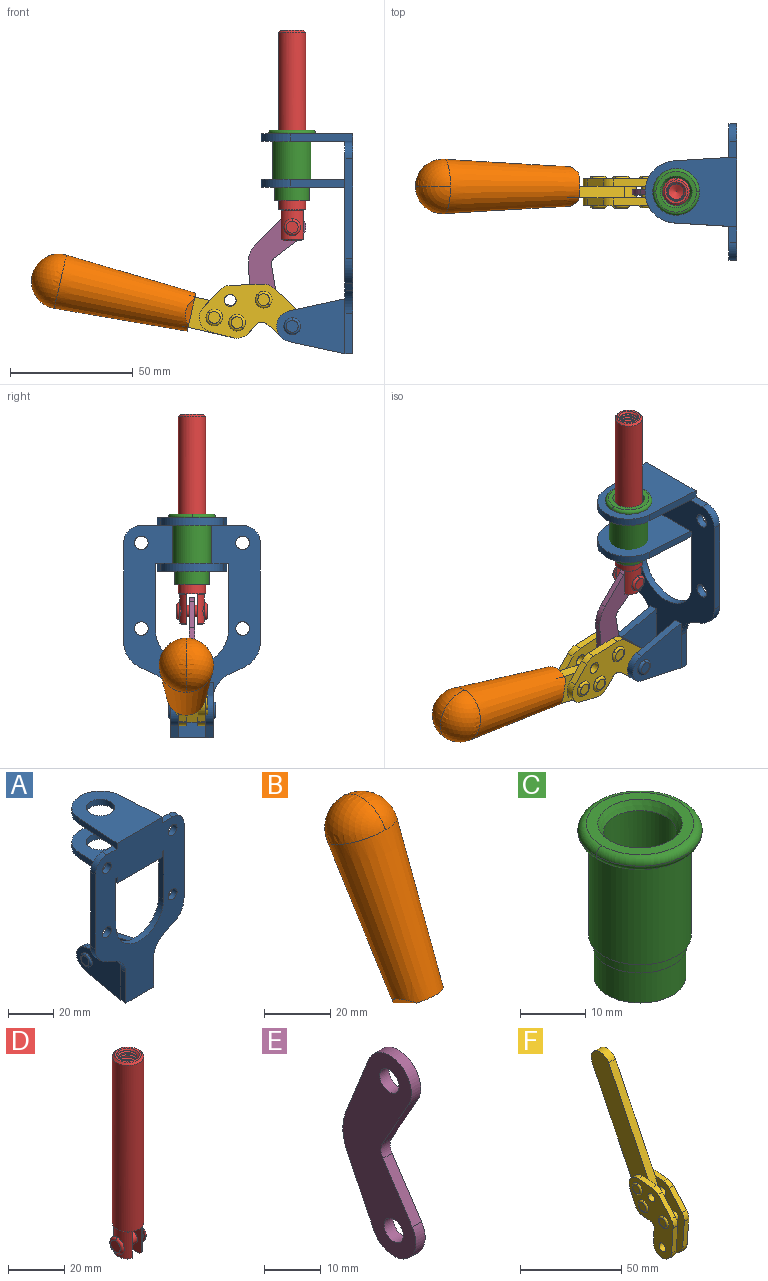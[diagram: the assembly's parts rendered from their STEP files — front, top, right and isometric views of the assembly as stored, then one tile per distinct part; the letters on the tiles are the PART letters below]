
ASSEMBLY  parts=6 mates=6
PART A: 55 faces, bbox 55.7x37.4x89.8 mm
  f0: torus R=2.41mm, axis (-1,0,0), area 15mm2, adj f11,f15,f25
  f1: torus R=2.41mm, axis (-1,0,0), area 15mm2, adj f10,f12,f22
  f2: cylinder r=2.78mm len=5.56mm, axis (0,-1,0), area 54.2mm2, adj f30,f54
  f3: cylinder r=14.99mm len=29.97mm, axis (0,-1,0), area 145.9mm2, adj f30,f49,f53,f54
  f4: cylinder r=2.78mm len=5.56mm, axis (0,-1,0), area 54.2mm2, adj f30,f54
  f5: cylinder r=2.78mm len=5.56mm, axis (0,-1,0), area 54.2mm2, adj f30,f54
  f6: cylinder r=2.78mm len=5.56mm, axis (0,-1,0), area 54.2mm2, adj f30,f54
  f7: cylinder r=6.35mm len=12.7mm, axis (0,0,1), area 123.6mm2, adj f27,f51
  f8: cylinder r=6.35mm len=12.7mm, axis (0,0,-1), area 124.7mm2, adj f21,f35
  f9: cylinder r=2.41mm len=11.18mm, axis (-1,0,0), area 169.4mm2, adj f16,f19
  f10: plane 4.83x4.83mm, normal (1,0,0), area 18.3mm2, adj f1,f12
  f11: plane 4.83x4.83mm, normal (-1,0,0), area 18.3mm2, adj f0,f15
  f12: torus R=2.41mm, axis (-1,0,0), area 15mm2, adj f1,f10,f22
  f13: cylinder r=6.35mm len=12.41mm, axis (1,0,0), area 53.4mm2, adj f18,f19,f22,f23
  f14: cylinder r=6.35mm len=12.41mm, axis (-1,0,0), area 53.4mm2, adj f16,f17,f24,f25
  f15: torus R=2.41mm, axis (-1,0,0), area 15mm2, adj f0,f11,f25
  f16: plane 27.86x22.35mm, normal (1,0,0), area 425.4mm2, adj f9,f14,f17,f24,f30
  f17: plane 22.86x4.97mm, normal (0,0.21,0.98), area 72.5mm2, adj f14,f16,f25,f30
  f18: plane 22.86x4.97mm, normal (0,0.21,0.98), area 72.5mm2, adj f13,f19,f22,f30
  f19: plane 27.86x22.35mm, normal (-1,0,0), area 425.4mm2, adj f9,f13,f18,f23,f30
  f20: cylinder r=12.7mm len=25.35mm, axis (0,0,-1), area 119.8mm2, adj f21,f34,f35,f36
  f21: plane 34.21x28.07mm, normal (0,0,-1), area 702.4mm2, adj f8,f20,f30,f34,f36
  f22: plane 27.96x22.45mm, normal (1,0,0), area 407.2mm2, adj f1,f12,f13,f18,f23,f30,f42,f43
  f23: plane 22.86x4.97mm, normal (0,0.21,-0.98), area 72.5mm2, adj f13,f19,f22,f44
  f24: plane 22.86x4.97mm, normal (0,0.21,-0.98), area 72.5mm2, adj f14,f16,f25,f44
  f25: plane 27.86x22.35mm, normal (-1,0,0), area 407.1mm2, adj f0,f14,f15,f17,f24,f30,f45,f46
  f26: plane 3.1x0.95mm, normal (0,0,-1), area 2.7mm2, adj f30,f49,f50,f54
  f27: plane 34.21x28.07mm, normal (0,0,1), area 702.4mm2, adj f7,f28,f30,f50,f52
  f28: cylinder r=12.7mm len=25.35mm, axis (0,0,1), area 118.8mm2, adj f27,f50,f51,f52
  f29: plane 3.1x0.95mm, normal (0,0,-1), area 2.7mm2, adj f30,f52,f53,f54
  f30: plane 86.54x55.63mm, normal (0,1,0), area 2362.9mm2, adj f2,f3,f4,f5,f6,f16,f17,f18
  f31: plane 40.56x3.1mm, normal (-1,0,0), area 125.7mm2, adj f30,f32,f48,f54
  f32: cylinder r=7.11mm len=7.11mm, axis (0,-1,0), area 34.6mm2, adj f30,f31,f33,f54
  f33: plane 6.67x3.1mm, normal (0,0,1), area 20.4mm2, adj f30,f32,f34,f54
  f34: plane 25.39x3.13mm, normal (-1,0.06,0), area 79.5mm2, adj f20,f21,f33,f35,f54
  f35: plane 37.31x28.45mm, normal (0,0,1), area 789.9mm2, adj f8,f20,f34,f36,f54
  f36: plane 25.39x3.13mm, normal (1,0.06,0), area 79.5mm2, adj f20,f21,f35,f37,f54
  f37: plane 6.67x3.1mm, normal (0,0,1), area 20.4mm2, adj f30,f36,f38,f54
  f38: cylinder r=7.11mm len=7.11mm, axis (0,-1,0), area 34.6mm2, adj f30,f37,f39,f54
  f39: plane 40.56x3.1mm, normal (1,0,0), area 125.7mm2, adj f30,f38,f40,f54
  f40: cylinder r=11.18mm len=10.16mm, axis (0,-1,0), area 39.5mm2, adj f30,f39,f41,f54
  f41: plane 6.09x3.1mm, normal (0.42,0,-0.91), area 20.8mm2, adj f30,f40,f42,f54
  f42: cylinder r=11.18mm len=9.41mm, axis (0,-1,0), area 37.2mm2, adj f22,f30,f41,f43,f54
  f43: plane 16.5x3.1mm, normal (1,0,0), area 51.1mm2, adj f22,f42,f44,f54
  f44: plane 17.37x3.1mm, normal (0,0,-1), area 53.8mm2, adj f23,f24,f30,f43,f45,f54
  f45: plane 16.5x3.1mm, normal (-1,0,0), area 51.1mm2, adj f25,f44,f46,f54
  f46: cylinder r=11.18mm len=9.41mm, axis (0,-1,0), area 37.2mm2, adj f25,f30,f45,f47,f54
  f47: plane 6.09x3.1mm, normal (-0.42,0,-0.91), area 20.8mm2, adj f30,f46,f48,f54
  f48: cylinder r=11.18mm len=10.16mm, axis (0,-1,0), area 39.5mm2, adj f30,f31,f47,f54
  f49: plane 26.54x3.1mm, normal (-1,0,0), area 82.3mm2, adj f3,f26,f30,f54
  f50: plane 25.39x3.1mm, normal (1,0.06,0), area 78.8mm2, adj f26,f27,f28,f51,f54
  f51: plane 37.31x28.45mm, normal (0,0,-1), area 789.9mm2, adj f7,f28,f50,f52,f54
  f52: plane 25.39x3.1mm, normal (-1,0.06,0), area 78.8mm2, adj f27,f28,f29,f51,f54
  f53: plane 26.54x3.1mm, normal (1,0,0), area 82.3mm2, adj f3,f29,f30,f54
  f54: plane 89.66x55.63mm, normal (0,-1,0), area 2678.5mm2, adj f2,f3,f4,f5,f6,f26,f29,f31
PART B: 11 faces, bbox 22.3x42.6x64.5 mm
  f0: sphere r=11.13mm, area 411.4mm2, adj f1,f8
  f1: cone r=11.11mm half-angle=3.3deg, axis (0,0.44,0.9), area 3251.8mm2, adj f0,f7,f8,f9,f10
  f2: cylinder r=6.16mm len=11.7mm, axis (1,0,0), area 89.5mm2, adj f3,f4,f5,f6
  f3: plane 60.23x36.75mm, normal (-1,0,0), area 763.6mm2, adj f2,f4,f6,f10
  f4: plane 51.37x25.05mm, normal (0,0.9,-0.44), area 264.2mm2, adj f2,f3,f5,f10
  f5: plane 60.23x36.75mm, normal (1,0,0), area 763.6mm2, adj f2,f4,f6,f10
  f6: plane 51.37x25.05mm, normal (0,-0.9,0.44), area 264.2mm2, adj f2,f3,f5,f10
  f7: plane 9.95x5.95mm, normal (0.71,-0.31,-0.64), area 25.8mm2, adj f1,f10
  f8: sphere r=11.13mm, area 411.4mm2, adj f0,f1
  f9: plane 9.95x5.95mm, normal (-0.71,-0.31,-0.64), area 25.8mm2, adj f1,f10
  f10: plane 14.27x11.38mm, normal (0,-0.44,-0.9), area 106.7mm2, adj f1,f3,f4,f5,f6,f7,f9
PART C: 15 faces, bbox 20.6x20.6x28.7 mm
  f0: torus R=8.26mm, axis (0,0,1), area 56.8mm2, adj f1,f10,f12
  f1: torus R=8.26mm, axis (0,0,1), area 56.8mm2, adj f0,f6,f13
  f2: cylinder r=5.59mm len=25.91mm, axis (0,0,1), area 909.6mm2, adj f3,f4
  f3: cone r=6.86mm half-angle=45deg, axis (0,0,-1), area 70.2mm2, adj f2,f14
  f4: cone r=6.47mm half-angle=30deg, axis (0,0,1), area 66.7mm2, adj f2,f13
  f5: cylinder r=7.04mm len=14.07mm, axis (0,0,1), area 252.6mm2, adj f11,f14
  f6: torus R=8.26mm, axis (0,0,1), area 56.8mm2, adj f1,f12,f13
  f7: cylinder r=7.16mm len=14.33mm, axis (0,0,1), area 91.5mm2, adj f9,f11
  f8: cylinder r=7.86mm len=18.42mm, axis (0,0,1), area 909.6mm2, adj f9,f10
  f9: plane 15.72x15.72mm, normal (0,0,-1), area 33mm2, adj f7,f8
  f10: plane 16.51x16.51mm, normal (0,0,-1), area 19.9mm2, adj f0,f8,f12
  f11: plane 14.33x14.33mm, normal (0,0,-1), area 5.7mm2, adj f5,f7
  f12: torus R=8.26mm, axis (0,0,1), area 56.8mm2, adj f0,f6,f10
  f13: plane 16.51x16.51mm, normal (0,0,1), area 82.7mm2, adj f1,f4,f6
  f14: plane 14.07x14.07mm, normal (0,0,-1), area 7.8mm2, adj f3,f5
PART D: 48 faces, bbox 12.6x11.1x86.1 mm
  f0: torus R=2.41mm, axis (-1,0,0), area 15mm2, adj f30,f32,f34
  f1: torus R=2.41mm, axis (-1,0,0), area 15mm2, adj f29,f31,f33
  f2: cylinder r=5.54mm len=72.39mm, axis (0,0,1), area 2518.5mm2, adj f3,f4,f42,f43
  f3: cone r=5.54mm half-angle=45deg, axis (0,0,1), area 7.6mm2, adj f2,f5,f41
  f4: cone r=5.54mm half-angle=45deg, axis (0,0,-1), area 34.9mm2, adj f2,f39
  f5: cylinder r=5.08mm len=11.48mm, axis (0,0,1), area 108.3mm2, adj f3,f7,f8,f41
  f6: cylinder r=2.41mm len=4.83mm, axis (-1,0,0), area 71.2mm2, adj f40,f41
  f7: cylinder r=2.41mm len=4.83mm, axis (-1,0,0), area 7.6mm2, adj f5,f34
  f8: cone r=5.08mm half-angle=45deg, axis (0,0,1), area 10.6mm2, adj f5,f37,f41
  f9: cone r=3.98mm half-angle=45deg, axis (0,0,1), area 17.6mm2, adj f27,f39,f45,f46,f47
  f10: cylinder r=2.41mm len=4.83mm, axis (-1,0,0), area 7.6mm2, adj f33,f38
  f11: cylinder r=3.2mm len=6.4mm, axis (0,0,1), area 78.4mm2, adj f12,f28,f44,f45,f47
  f12: cylinder r=3.2mm len=6.4mm, axis (0,0,1), area 10.5mm2, adj f11,f13,f45,f47
  f13: cylinder r=3.2mm len=6.4mm, axis (0,0,1), area 10.5mm2, adj f12,f14,f45,f47
  f14: cylinder r=3.2mm len=6.4mm, axis (0,0,1), area 10.5mm2, adj f13,f15,f45,f47
  f15: cylinder r=3.2mm len=6.4mm, axis (0,0,1), area 10.5mm2, adj f14,f16,f45,f47
  f16: cylinder r=3.2mm len=6.4mm, axis (0,0,1), area 10.5mm2, adj f15,f17,f45,f47
  f17: cylinder r=3.2mm len=6.4mm, axis (0,0,1), area 10.5mm2, adj f16,f18,f45,f47
  f18: cylinder r=3.2mm len=6.4mm, axis (0,0,1), area 10.5mm2, adj f17,f19,f45,f47
  f19: cylinder r=3.2mm len=6.4mm, axis (0,0,1), area 10.5mm2, adj f18,f20,f45,f47
  f20: cylinder r=3.2mm len=6.4mm, axis (0,0,1), area 10.5mm2, adj f19,f21,f45,f47
  f21: cylinder r=3.2mm len=6.4mm, axis (0,0,1), area 10.5mm2, adj f20,f22,f45,f47
  f22: cylinder r=3.2mm len=6.4mm, axis (0,0,1), area 10.5mm2, adj f21,f23,f45,f47
  f23: cylinder r=3.2mm len=6.4mm, axis (0,0,1), area 10.5mm2, adj f22,f24,f45,f47
  f24: cylinder r=3.2mm len=6.4mm, axis (0,0,1), area 10.5mm2, adj f23,f25,f45,f47
  f25: cylinder r=3.2mm len=6.4mm, axis (0,0,1), area 10.5mm2, adj f24,f26,f45,f47
  f26: cylinder r=3.2mm len=6.4mm, axis (0,0,1), area 10.5mm2, adj f25,f27,f45,f47
  f27: cylinder r=3.2mm len=6.4mm, axis (0,0,1), area 7.4mm2, adj f9,f26,f45,f47
  f28: cone r=3.2mm half-angle=60deg, axis (0,0,1), area 37.2mm2, adj f11
  f29: plane 4.83x4.83mm, normal (-1,0,0), area 18.3mm2, adj f1,f31
  f30: plane 4.83x4.83mm, normal (1,0,0), area 18.3mm2, adj f0,f32
  f31: torus R=2.41mm, axis (-1,0,0), area 15mm2, adj f1,f29,f33
  f32: torus R=2.41mm, axis (-1,0,0), area 15mm2, adj f0,f30,f34
  f33: plane 6.83x6.83mm, normal (1,0,0), area 18.3mm2, adj f1,f10,f31
  f34: plane 6.83x6.83mm, normal (-1,0,0), area 18.3mm2, adj f0,f7,f32
  f35: cone r=5.08mm half-angle=45deg, axis (0,0,1), area 10.6mm2, adj f36,f38,f40
  f36: plane 7.25x1.97mm, normal (0,0,-1), area 10mm2, adj f35,f40
  f37: plane 7.25x1.97mm, normal (0,0,-1), area 10mm2, adj f8,f41
  f38: cylinder r=5.08mm len=11.48mm, axis (0,0,1), area 108.3mm2, adj f10,f35,f40,f42
  f39: plane 9.55x9.55mm, normal (0,0,1), area 22mm2, adj f4,f9
  f40: plane 12.76x10.09mm, normal (1,0,0), area 95.7mm2, adj f6,f35,f36,f38,f42,f43
  f41: plane 12.76x10.09mm, normal (-1,0,0), area 95.7mm2, adj f3,f5,f6,f8,f37,f43
  f42: cone r=5.54mm half-angle=45deg, axis (0,0,1), area 7.6mm2, adj f2,f38,f40
  f43: plane 11.07x4.7mm, normal (0,0,-1), area 50.4mm2, adj f2,f40,f41
  f44: plane 0.89x0.62mm, normal (-1,0,0), area 0.3mm2, adj f11,f45,f46,f47
  f45: bspline ~24.8x7.63mm, area 266.6mm2, adj f9,f11,f12,f13,f14,f15,f16,f17
  f46: bspline ~24.87x7.63mm, area 73.6mm2, adj f9,f44,f45,f47
  f47: bspline ~24.98x7.63mm, area 272.5mm2, adj f9,f11,f12,f13,f14,f15,f16,f17
PART E: 12 faces, bbox 2.3x18.2x42.8 mm
  f0: cylinder r=2.4mm len=4.8mm, axis (1,0,0), area 34.9mm2, adj f4,f11
  f1: cylinder r=10.41mm len=8.47mm, axis (1,0,0), area 20.2mm2, adj f4,f9,f10,f11
  f2: cylinder r=3.05mm len=3.16mm, axis (1,0,0), area 7.7mm2, adj f4,f6,f7,f11
  f3: cylinder r=2.4mm len=4.8mm, axis (1,0,0), area 34.9mm2, adj f4,f11
  f4: plane 42.81x18.23mm, normal (-1,0,0), area 414.1mm2, adj f0,f1,f2,f3,f5,f6,f7,f8
  f5: cylinder r=5.54mm len=10.67mm, axis (1,0,0), area 41.8mm2, adj f4,f6,f10,f11
  f6: plane 11.66x6.53mm, normal (0,-0.87,-0.49), area 30.9mm2, adj f2,f4,f5,f11
  f7: plane 11.17x7.33mm, normal (0,-0.84,0.55), area 30.9mm2, adj f2,f4,f8,f11
  f8: cylinder r=5.54mm len=10.51mm, axis (1,0,0), area 41.8mm2, adj f4,f7,f9,f11
  f9: plane 13.67x6.67mm, normal (0,0.9,-0.44), area 35.1mm2, adj f1,f4,f8,f11
  f10: plane 14.1x5.7mm, normal (0,0.93,0.37), area 35.1mm2, adj f1,f4,f5,f11
  f11: plane 42.81x18.23mm, normal (1,0,0), area 414.1mm2, adj f0,f1,f2,f3,f5,f6,f7,f8
PART F: 59 faces, bbox 12.9x60.2x99.6 mm
  f0: torus R=2.39mm, axis (-1,0,0), area 14.9mm2, adj f20,f43,f51
  f1: torus R=2.39mm, axis (-1,0,0), area 14.9mm2, adj f19,f42,f51
  f2: torus R=2.39mm, axis (-1,0,0), area 14.9mm2, adj f18,f35,f51
  f3: torus R=2.39mm, axis (-1,0,0), area 14.9mm2, adj f14,f17,f23
  f4: torus R=2.39mm, axis (-1,0,0), area 14.9mm2, adj f13,f16,f23
  f5: torus R=2.39mm, axis (-1,0,0), area 14.9mm2, adj f12,f15,f23
  f6: cylinder r=2.39mm len=4.78mm, axis (1,0,0), area 46.5mm2, adj f48,f50,f51
  f7: cylinder r=2.39mm len=4.78mm, axis (1,0,0), area 46.5mm2, adj f50,f51
  f8: cylinder r=6.35mm len=12.68mm, axis (1,0,0), area 61.8mm2, adj f38,f39,f50,f51
  f9: cylinder r=2.39mm len=4.78mm, axis (-1,0,0), area 70.5mm2, adj f46,f50
  f10: cylinder r=2.39mm len=4.78mm, axis (-1,0,0), area 46.5mm2, adj f23,f45,f46
  f11: cylinder r=2.39mm len=4.78mm, axis (-1,0,0), area 46.5mm2, adj f23,f46
  f12: plane 4.78x4.78mm, normal (1,0,0), area 17.9mm2, adj f5,f15
  f13: plane 4.78x4.78mm, normal (1,0,0), area 17.9mm2, adj f4,f16
  f14: plane 4.78x4.78mm, normal (1,0,0), area 17.9mm2, adj f3,f17
  f15: torus R=2.39mm, axis (-1,0,0), area 14.9mm2, adj f5,f12,f23
  f16: torus R=2.39mm, axis (-1,0,0), area 14.9mm2, adj f4,f13,f23
  f17: torus R=2.39mm, axis (-1,0,0), area 14.9mm2, adj f3,f14,f23
  f18: plane 4.78x4.78mm, normal (-1,0,0), area 17.9mm2, adj f2,f35
  f19: plane 4.78x4.78mm, normal (-1,0,0), area 17.9mm2, adj f1,f42
  f20: plane 4.78x4.78mm, normal (-1,0,0), area 17.9mm2, adj f0,f43
  f21: plane 2.26x0.2mm, normal (1,0,0), area 0.2mm2, adj f31,f44
  f22: plane 2.26x0.2mm, normal (-1,0,0), area 0.2mm2, adj f41,f44
  f23: plane 39.37x30.77mm, normal (1,0,0), area 565.5mm2, adj f3,f4,f5,f10,f11,f15,f16,f17
  f24: cylinder r=6.1mm len=4.15mm, axis (-1,0,0), area 14.7mm2, adj f23,f25,f32,f46
  f25: plane 10.25x9.01mm, normal (0,-0.75,0.66), area 42.3mm2, adj f23,f24,f26,f46
  f26: cylinder r=6.35mm len=4.64mm, axis (-1,0,0), area 15.6mm2, adj f23,f25,f27,f46
  f27: plane 15.84x3.1mm, normal (0,-1,-0.07), area 49.2mm2, adj f23,f26,f28,f46
  f28: cylinder r=6.35mm len=12.68mm, axis (-1,0,0), area 61.8mm2, adj f23,f27,f29,f46
  f29: plane 8.11x3.1mm, normal (0,1,0.07), area 25.2mm2, adj f23,f28,f30,f46
  f30: cylinder r=3.05mm len=3.25mm, axis (-1,0,0), area 14.8mm2, adj f23,f29,f31,f46
  f31: plane 5.99x3.1mm, normal (0,0.07,-1), area 18.6mm2, adj f21,f23,f30,f44,f46
  f32: plane 9.5x3.1mm, normal (0,-0.07,1), area 29.5mm2, adj f23,f24,f33,f46,f47
  f33: cylinder r=6.1mm len=8.63mm, axis (-1,0,0), area 39.1mm2, adj f23,f32,f34,f47
  f34: plane 8.65x3.96mm, normal (0,0.91,-0.42), area 29.5mm2, adj f23,f33,f44,f47
  f35: torus R=2.39mm, axis (-1,0,0), area 14.9mm2, adj f2,f18,f51
  f36: plane 10.25x9.01mm, normal (0,-0.75,0.66), area 42.3mm2, adj f37,f49,f50,f51
  f37: cylinder r=6.35mm len=4.64mm, axis (1,0,0), area 15.6mm2, adj f36,f38,f50,f51
  f38: plane 15.84x3.1mm, normal (0,-1,-0.07), area 49.2mm2, adj f8,f37,f50,f51
  f39: plane 8.11x3.1mm, normal (0,1,0.07), area 25.2mm2, adj f8,f40,f50,f51
  f40: cylinder r=3.05mm len=3.25mm, axis (1,0,0), area 14.8mm2, adj f39,f41,f50,f51
  f41: plane 5.99x3.1mm, normal (0,0.07,-1), area 18.6mm2, adj f22,f40,f44,f50,f51
  f42: torus R=2.39mm, axis (-1,0,0), area 14.9mm2, adj f1,f19,f51
  f43: torus R=2.39mm, axis (-1,0,0), area 14.9mm2, adj f0,f20,f51
  f44: cylinder r=6.35mm len=12.12mm, axis (-1,0,0), area 128.9mm2, adj f21,f22,f23,f31,f34,f41,f46,f47
  f45: plane 2.65x1.35mm, normal (1,0,0), area 1mm2, adj f10,f55
  f46: plane 39.08x20.42mm, normal (-1,0,0), area 412.5mm2, adj f9,f10,f11,f24,f25,f26,f27,f28
  f47: plane 77.62x39.82mm, normal (1,0,0), area 850mm2, adj f32,f33,f34,f44,f53,f54,f55
  f48: plane 2.65x1.35mm, normal (-1,0,0), area 1mm2, adj f6,f55
  f49: cylinder r=6.1mm len=4.15mm, axis (1,0,0), area 14.7mm2, adj f36,f50,f51,f56
  f50: plane 39.08x20.42mm, normal (1,0,0), area 412.5mm2, adj f6,f7,f8,f9,f36,f37,f38,f39
  f51: plane 39.37x30.77mm, normal (-1,0,0), area 565.5mm2, adj f0,f1,f2,f6,f7,f8,f35,f36
  f52: plane 8.65x3.96mm, normal (0,0.91,-0.42), area 29.5mm2, adj f44,f51,f57,f58
  f53: plane 68.49x33.4mm, normal (0,0.9,-0.44), area 358.1mm2, adj f44,f47,f54,f58
  f54: cylinder r=6.35mm len=12.06mm, axis (1,0,0), area 93.7mm2, adj f47,f53,f55,f58
  f55: plane 68.49x33.4mm, normal (0,-0.9,0.44), area 358.1mm2, adj f44,f45,f46,f47,f48,f50,f54,f58
  f56: plane 9.5x3.1mm, normal (0,-0.07,1), area 29.5mm2, adj f49,f50,f51,f57,f58
  f57: cylinder r=6.1mm len=8.63mm, axis (1,0,0), area 39.1mm2, adj f51,f52,f56,f58
  f58: plane 77.62x39.82mm, normal (-1,0,0), area 850mm2, adj f44,f52,f53,f54,f55,f56,f57
PLACE A rot(axis=(0,0,1),90deg) t=(0,0,-1.23)mm fixed
PLACE B rot(axis=(-0.4,-0.4,0.83),100.7deg) t=(-34.03,2.31,6.01)mm
PLACE C rot(axis=(0,0,1),180deg) t=(-24.61,24.61,-2.25)mm
PLACE D rot(axis=(0,0,1),90deg) t=(0,0,-8.41)mm
PLACE E rot(axis=(0.2,0.2,0.96),92.4deg) t=(-8.18,0,-16.92)mm
PLACE F rot(axis=(-0.4,-0.4,0.83),100.7deg) t=(-34.03,0,6.01)mm
MATE fastened C.f2 <-> A.f7  axis (0,0,1) through (-24.61,0,45.16)mm
MATE revolute F.f7 <-> A.f0  axis (0,-1,0) through (-24.61,0,-33.32)mm
MATE slider D.f2 <-> C.f2  axis (0,0,1) through (-24.61,0,50.38)mm
MATE fastened B.f2 <-> F.f54  axis (0,1,0) through (-121.32,0,-14.64)mm
MATE revolute E.f5 <-> D.f6  axis (0,1,0) through (-24.61,0,7.07)mm
MATE revolute E.f3 <-> F.f4  axis (0,1,0) through (-36.21,0,-22.49)mm
